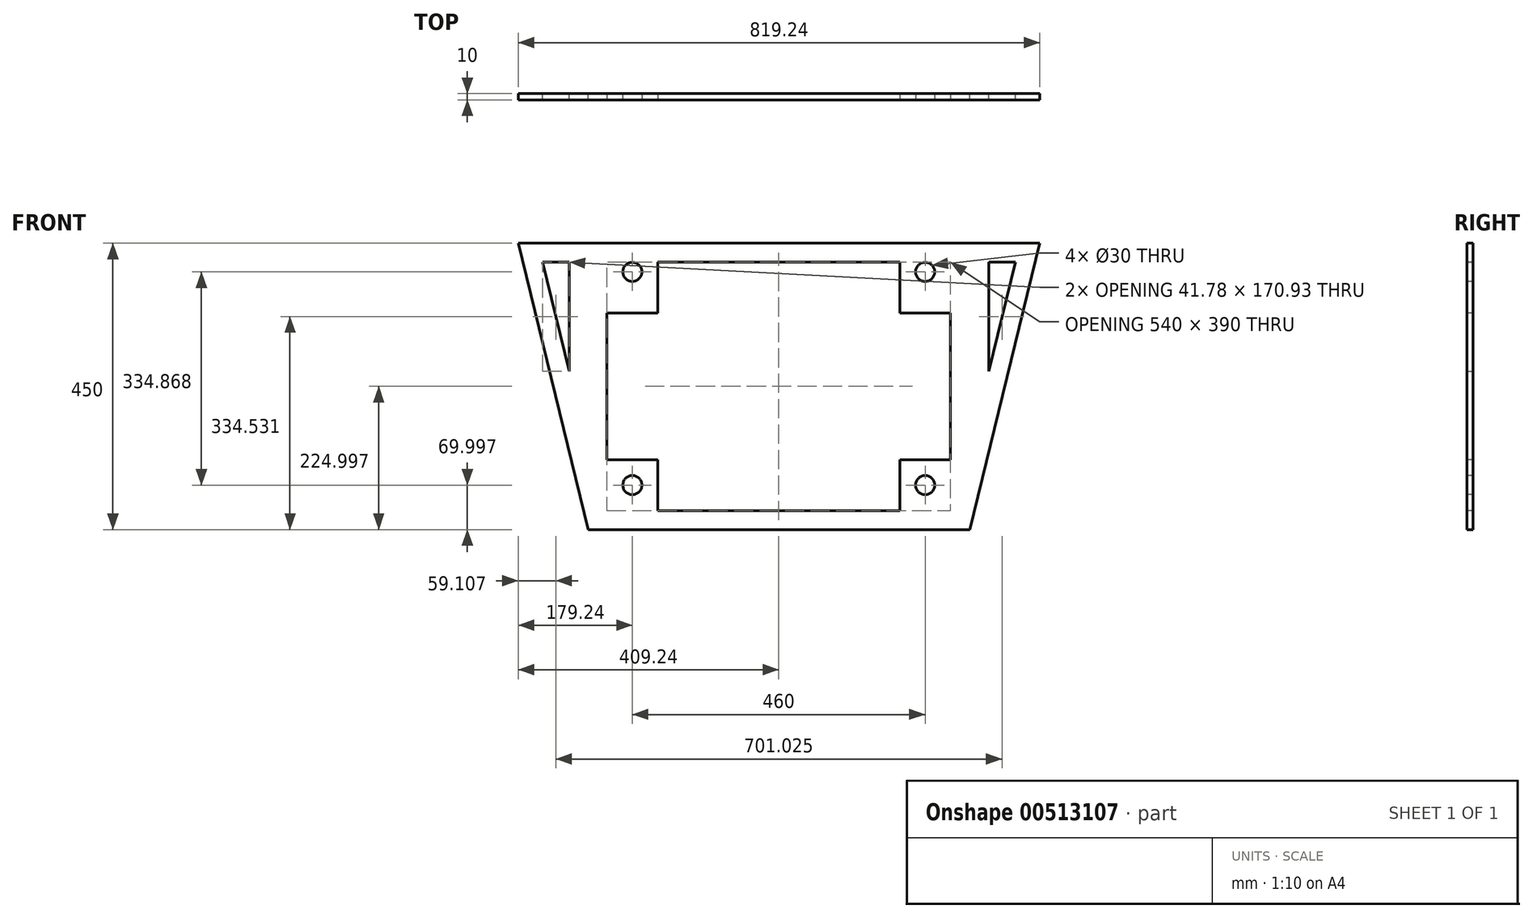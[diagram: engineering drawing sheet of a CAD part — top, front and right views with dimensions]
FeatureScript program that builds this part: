
annotation { "Feature Type Name" : "Feature", "Feature Type Description" : "" }
export const myFeature = defineFeature(function(context is Context, id is Id, definition is map)
    precondition{}
    {
        {
            var Q0;
            Q0=qCreatedBy(makeId("Front.planeOp"),FACE);
            var sketch = newSketch(context, id + "F0", { "sketchPlane" : qUnion([Q0])});
            skLineSegment(sketch, "E0.1", {"start": v(-436.34, 213.95) * mm, "end": v(-436.34, -176.05) * mm});
            skLineSegment(sketch, "E0.3", {"start": v(103.66, 213.95) * mm, "end": v(103.66, -176.05) * mm});
            skLineSegment(sketch, "E1", {"start": v(-465.58, -206.05) * mm, "end": v(133.66, -206.05) * mm});
            skLineSegment(sketch, "E2", {"start": v(-436.34, -176.05) * mm, "end": v(103.66, -176.05) * mm});
            skLineSegment(sketch, "E3", {"start": v(-436.34, 213.95) * mm, "end": v(103.66, 213.95) * mm});
            skLineSegment(sketch, "E4", {"start": v(-465.58, 243.95) * mm, "end": v(133.66, 243.95) * mm});
            skLineSegment(sketch, "E5", {"start": v(-465.58, 243.95) * mm, "end": v(-575.58, 243.95) * mm});
            skLineSegment(sketch, "E6", {"start": v(133.66, 243.95) * mm, "end": v(243.66, 243.95) * mm});
            skLineSegment(sketch, "E7", {"start": v(-575.58, 243.95) * mm, "end": v(-465.58, -206.05) * mm});
            skLineSegment(sketch, "E8", {"start": v(243.66, 243.95) * mm, "end": v(133.66, -206.05) * mm});
            skLineSegment(sketch, "E9.0", {"start": v(-537.36, 213.95) * mm, "end": v(-495.58, 43.02) * mm});
            skLineSegment(sketch, "E9.1", {"start": v(-495.58, 213.95) * mm, "end": v(-537.36, 213.95) * mm});
            skLineSegment(sketch, "E9.2", {"start": v(-495.58, 213.95) * mm, "end": v(-495.58, 43.02) * mm});
            skLineSegment(sketch, "E10.0", {"start": v(205.44, 213.95) * mm, "end": v(163.66, 43.02) * mm});
            skLineSegment(sketch, "E10.1", {"start": v(163.66, 213.95) * mm, "end": v(205.44, 213.95) * mm});
            skLineSegment(sketch, "E10.2", {"start": v(163.66, 213.95) * mm, "end": v(163.66, 43.02) * mm});
            skSolve(sketch);
        }
        {
            var Q0;
            Q0=makeQuery(id+"F0.imprint","IMPRINT",FACE,{"disambiguationData":[TD([[makeQuery(id+"F0.imprint","IMPRINT",EDGE,{"derivedFrom":sQuery(id+"F0.wireOp",EDGE,"E0.1")}),-1.0]])]});
            extrude(context, id + "F1", {"entities" : qUnion([Q0]), "depth" : 10 * mm, "offsetDistance" : 25 * mm});
        }
        {
            var Q0;
            Q0=makeQuery(id+"F1.opExtrude","CAP_FACE",FACE,{"disambiguationData":[OSD([sQuery(id+"F0.wireOp",EDGE,"E0.1"),sQuery(id+"F0.wireOp",EDGE,"E0.3"),sQuery(id+"F0.wireOp",EDGE,"E1"),sQuery(id+"F0.wireOp",EDGE,"E2"),sQuery(id+"F0.wireOp",EDGE,"E3"),sQuery(id+"F0.wireOp",EDGE,"E4"),sQuery(id+"F0.wireOp",EDGE,"E5"),sQuery(id+"F0.wireOp",EDGE,"E6"),sQuery(id+"F0.wireOp",EDGE,"E7"),sQuery(id+"F0.wireOp",EDGE,"E8"),sQuery(id+"F0.wireOp",EDGE,"E9.0"),sQuery(id+"F0.wireOp",EDGE,"E9.1"),sQuery(id+"F0.wireOp",EDGE,"E9.2"),sQuery(id+"F0.wireOp",EDGE,"E10.0"),sQuery(id+"F0.wireOp",EDGE,"E10.1"),sQuery(id+"F0.wireOp",EDGE,"E10.2")])],"isStart":false});
            var sketch = newSketch(context, id + "F2", { "sketchPlane" : qUnion([Q0])});
            skLineSegment(sketch, "E11.bottom", {"start": v(-436.34, 213.95) * mm, "end": v(-356.34, 213.95) * mm});
            skLineSegment(sketch, "E11.top", {"start": v(-436.34, 133.95) * mm, "end": v(-356.34, 133.95) * mm});
            skLineSegment(sketch, "E11.left", {"start": v(-436.34, 213.95) * mm, "end": v(-436.34, 133.95) * mm});
            skLineSegment(sketch, "E11.right", {"start": v(-356.34, 213.95) * mm, "end": v(-356.34, 133.95) * mm});
            skLineSegment(sketch, "E12.bottom", {"start": v(103.66, 213.95) * mm, "end": v(23.66, 213.95) * mm});
            skLineSegment(sketch, "E12.top", {"start": v(103.66, 133.95) * mm, "end": v(23.66, 133.95) * mm});
            skLineSegment(sketch, "E12.left", {"start": v(103.66, 213.95) * mm, "end": v(103.66, 133.95) * mm});
            skLineSegment(sketch, "E12.right", {"start": v(23.66, 213.95) * mm, "end": v(23.66, 133.95) * mm});
            skLineSegment(sketch, "E13.bottom", {"start": v(-436.34, -176.05) * mm, "end": v(-356.34, -176.05) * mm});
            skLineSegment(sketch, "E13.top", {"start": v(-436.34, -96.05) * mm, "end": v(-356.34, -96.05) * mm});
            skLineSegment(sketch, "E13.left", {"start": v(-436.34, -176.05) * mm, "end": v(-436.34, -96.05) * mm});
            skLineSegment(sketch, "E13.right", {"start": v(-356.34, -176.05) * mm, "end": v(-356.34, -96.05) * mm});
            skLineSegment(sketch, "E14.bottom", {"start": v(103.66, -176.05) * mm, "end": v(23.66, -176.05) * mm});
            skLineSegment(sketch, "E14.top", {"start": v(103.66, -96.05) * mm, "end": v(23.66, -96.05) * mm});
            skLineSegment(sketch, "E14.left", {"start": v(103.66, -176.05) * mm, "end": v(103.66, -96.05) * mm});
            skLineSegment(sketch, "E14.right", {"start": v(23.66, -176.05) * mm, "end": v(23.66, -96.05) * mm});
            skCircle(sketch, "E15", {"center": v(-396.34, -136.05) * mm, "radius": 15 * mm});
            skCircle(sketch, "E16", {"center": v(-396.34, 198.82) * mm, "radius": 15 * mm});
            skCircle(sketch, "E17", {"center": v(63.66, 198.82) * mm, "radius": 15 * mm});
            skCircle(sketch, "E18", {"center": v(63.66, -136.05) * mm, "radius": 15 * mm});
            skSolve(sketch);
        }
        {
            var Q0;
            Q0=makeQuery(id+"F2.imprint","IMPRINT",FACE,{"disambiguationData":[TD([[makeQuery(id+"F2.imprint","IMPRINT",EDGE,{"derivedFrom":sQuery(id+"F2.wireOp",EDGE,"E11.bottom")}),-1.0]])]});
            var Q1;
            Q1=makeQuery(id+"F2.imprint","IMPRINT",FACE,{"disambiguationData":[TD([[makeQuery(id+"F2.imprint","IMPRINT",EDGE,{"derivedFrom":sQuery(id+"F2.wireOp",EDGE,"E12.bottom")}),-1.0]])]});
            var Q2;
            Q2=makeQuery(id+"F2.imprint","IMPRINT",FACE,{"disambiguationData":[TD([[makeQuery(id+"F2.imprint","IMPRINT",EDGE,{"derivedFrom":sQuery(id+"F2.wireOp",EDGE,"E14.bottom")}),1.0]])]});
            var Q3;
            Q3=makeQuery(id+"F2.imprint","IMPRINT",FACE,{"disambiguationData":[TD([[makeQuery(id+"F2.imprint","IMPRINT",EDGE,{"derivedFrom":sQuery(id+"F2.wireOp",EDGE,"E13.bottom")}),1.0]])]});
            extrude(context, id + "F3", {"entities" : qUnion([Q0, Q1, Q2, Q3]), "operationType" : NewBodyOperationType.ADD, "oppositeDirection" : true, "depth" : 10 * mm, "offsetDistance" : 25 * mm});
        }
    });
